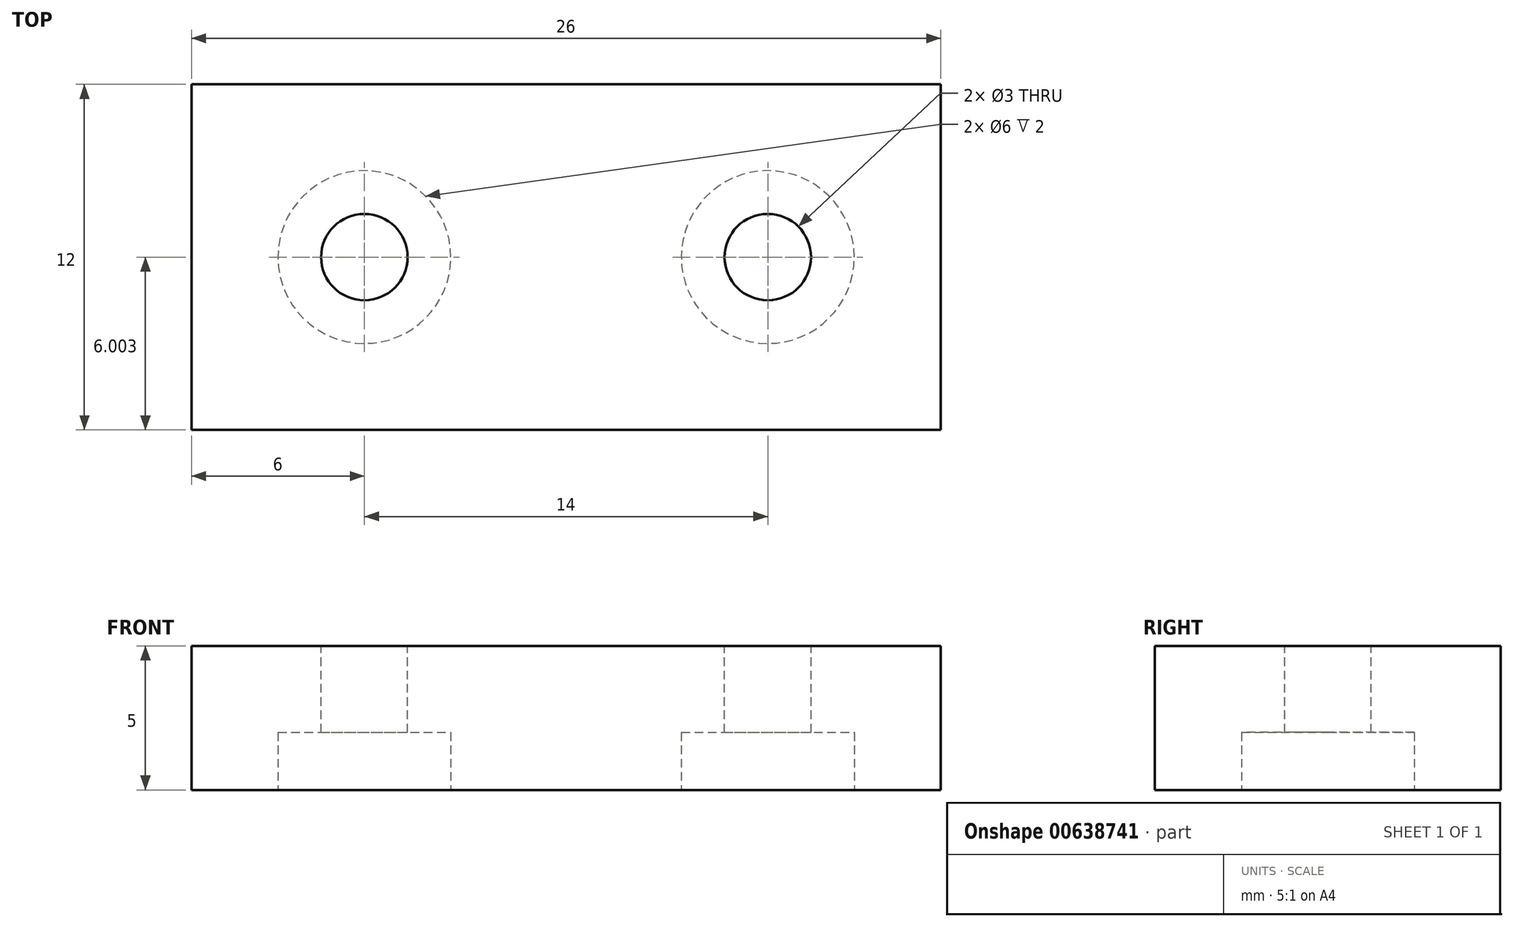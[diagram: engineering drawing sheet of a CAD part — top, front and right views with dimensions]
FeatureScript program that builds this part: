
annotation { "Feature Type Name" : "Feature", "Feature Type Description" : "" }
export const myFeature = defineFeature(function(context is Context, id is Id, definition is map)
    precondition{}
    {
        {
            var Q0;
            Q0=qCreatedBy(makeId("Top.planeOp"),FACE);
            var sketch = newSketch(context, id + "F0", { "sketchPlane" : qUnion([Q0])});
            skCircle(sketch, "E0", {"center": v(-70, -45.09) * mm, "radius": 1.5 * mm});
            skCircle(sketch, "E1", {"center": v(-84, -45.09) * mm, "radius": 1.5 * mm});
            skLineSegment(sketch, "E2.bottom", {"start": v(-90, -39.09) * mm, "end": v(-64, -39.09) * mm});
            skLineSegment(sketch, "E2.top", {"start": v(-90, -51.09) * mm, "end": v(-64, -51.09) * mm});
            skLineSegment(sketch, "E2.left", {"start": v(-90, -39.09) * mm, "end": v(-90, -51.09) * mm});
            skLineSegment(sketch, "E2.right", {"start": v(-64, -39.09) * mm, "end": v(-64, -51.09) * mm});
            skSolve(sketch);
        }
        {
            var Q0;
            Q0=makeQuery(id+"F0.imprint","IMPRINT",FACE,{"disambiguationData":[TD([[makeQuery(id+"F0.imprint","IMPRINT",EDGE,{"derivedFrom":sQuery(id+"F0.wireOp",EDGE,"E2.bottom")}),-1.0]])]});
            extrude(context, id + "F1", {"entities" : qUnion([Q0]), "oppositeDirection" : true, "depth" : 5 * mm, "offsetDistance" : 25 * mm});
        }
        {
            var Q0;
            Q0=makeQuery(id+"F1.opExtrude","CAP_FACE",FACE,{"disambiguationData":[OSD([sQuery(id+"F0.wireOp",EDGE,"E0"),sQuery(id+"F0.wireOp",EDGE,"E1"),sQuery(id+"F0.wireOp",EDGE,"E2.bottom"),sQuery(id+"F0.wireOp",EDGE,"E2.top"),sQuery(id+"F0.wireOp",EDGE,"E2.left"),sQuery(id+"F0.wireOp",EDGE,"E2.right")])],"isStart":false});
            var sketch = newSketch(context, id + "F2", { "sketchPlane" : qUnion([Q0])});
            skCircle(sketch, "E3", {"center": v(-84, 45.09) * mm, "radius": 3 * mm});
            skCircle(sketch, "E4", {"center": v(-70, 45.09) * mm, "radius": 3 * mm});
            skSolve(sketch);
        }
        {
            var Q0;
            Q0=qSketchRegion(id+"F2",true);
            extrude(context, id + "F3", {"entities" : qUnion([Q0]), "operationType" : NewBodyOperationType.REMOVE, "oppositeDirection" : true, "depth" : 2 * mm, "offsetDistance" : 25 * mm});
        }
    });
